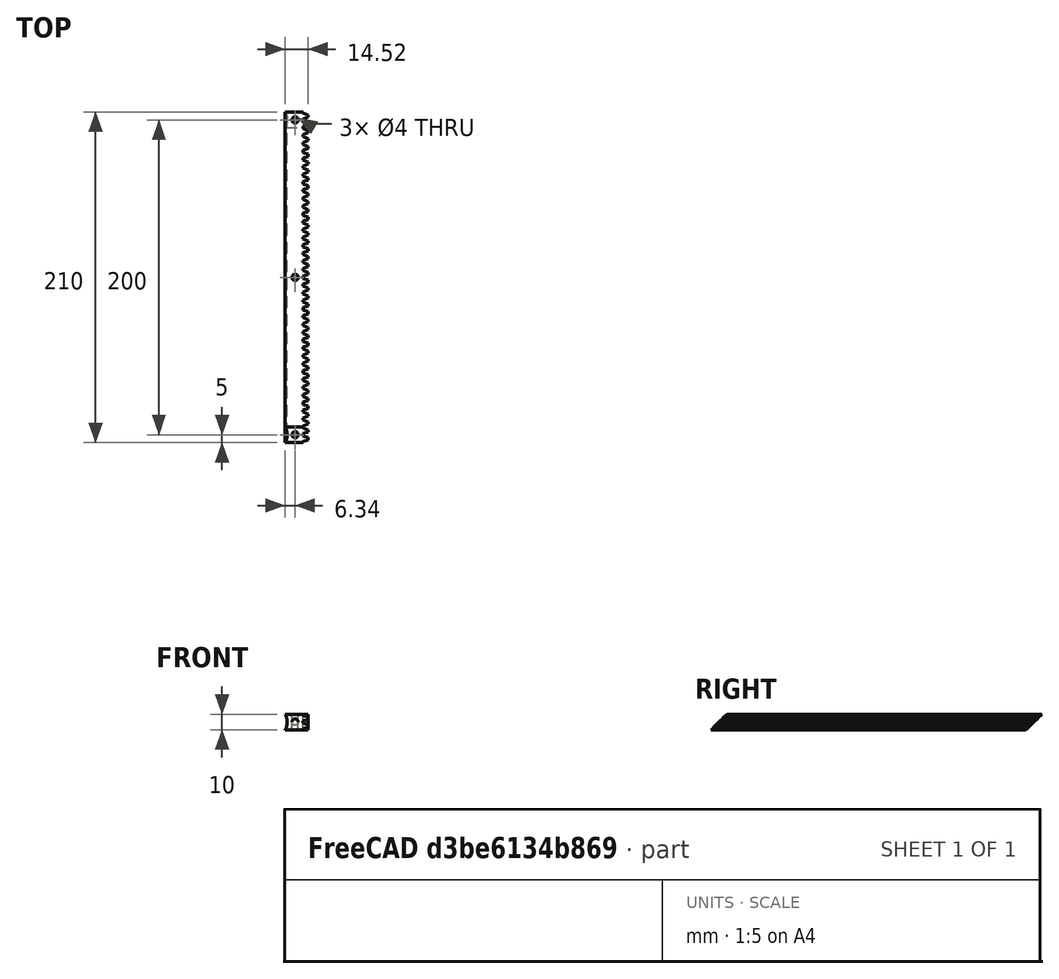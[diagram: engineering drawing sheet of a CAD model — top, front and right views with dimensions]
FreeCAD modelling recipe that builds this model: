
FCSTD DOCUMENT  (FreeCAD 0.17R13522 (Git))
Label: rack
License: All rights reserved
LicenseURL: http://en.wikipedia.org/wiki/All_rights_reserved
objects: Part::Cylinder×4, Part::Box×3, Part::MultiFuse×2, Part::FeaturePython×1, Part::Cut×1
note: 11 computed .brp shape members not serialized (recipe doc carries the construction recipe); baked Part::Feature solids carry a one-line shape summary decoded from their .brp

FEATURE [Part::FeaturePython] InvoluteRack  # WARN: FeaturePython — macro-defined, semantics opaque (R4)
  Placement = pos=(11.5915,2.5,-5) rot=(0,0,1;0rad)
  beta = 0
  double_helix = false
  head = 0
  height = 10
  module = 1.59155
  pressure_angle = 20
  teeth = 42
  thickness = 1
  expr: Placement.Base.x = 10 + 5 / pi
  expr: module = 5 / pi
FEATURE [Part::Box] Box  label="Cube"
  AttacherType = Attacher::AttachEngine3D
  Height = 10
  Length = 12
  Placement = pos=(-2,0,-5) rot=(0,0,1;0rad)
  Width = 210
FEATURE [Part::Cylinder] Cylinder
  Angle = 360
  AttacherType = Attacher::AttachEngine3D
  Height = 10
  Placement = pos=(5,5,-5) rot=(0,0,1;0rad)
  Radius = 2
FEATURE [Part::Cylinder] Cylinder001
  Angle = 360
  AttacherType = Attacher::AttachEngine3D
  Height = 10
  Placement = pos=(5,105,-5) rot=(0,0,1;0rad)
  Radius = 2
FEATURE [Part::Cylinder] Cylinder002
  Angle = 360
  AttacherType = Attacher::AttachEngine3D
  Height = 10
  Placement = pos=(5,205,-5) rot=(0,0,1;0rad)
  Radius = 2
FEATURE [Part::MultiFuse] Fusion  label="Positive Fusion"
  Shapes = -> [Box,InvoluteRack]
FEATURE [Part::Cylinder] Cylinder003  label="Rail"
  Angle = 360
  AttacherType = Attacher::AttachEngine3D
  Height = 210
  Placement = pos=(-10,0,0) rot=(-1,0,0;1.5708rad)
  Radius = 10
FEATURE [Part::Box] Box001  label="Cube001"
  AttacherType = Attacher::AttachEngine3D
  Height = 20
  Length = 20
  Placement = pos=(-5,10,5) rot=(1,0,0;2.35619rad)
  Width = 10
FEATURE [Part::Box] Box002  label="Cube002"
  AttacherType = Attacher::AttachEngine3D
  Height = 20
  Length = 20
  Placement = pos=(-5,200,-5) rot=(-1,0,0;0.785398rad)
  Width = 10
FEATURE [Part::MultiFuse] Fusion001  label="Negative Fusion"
  Shapes = -> [Cylinder,Cylinder001,Cylinder002,Cylinder003,Box001,Box002]
FEATURE [Part::Cut] Cut
  Base = -> Fusion
  Tool = -> Fusion001
